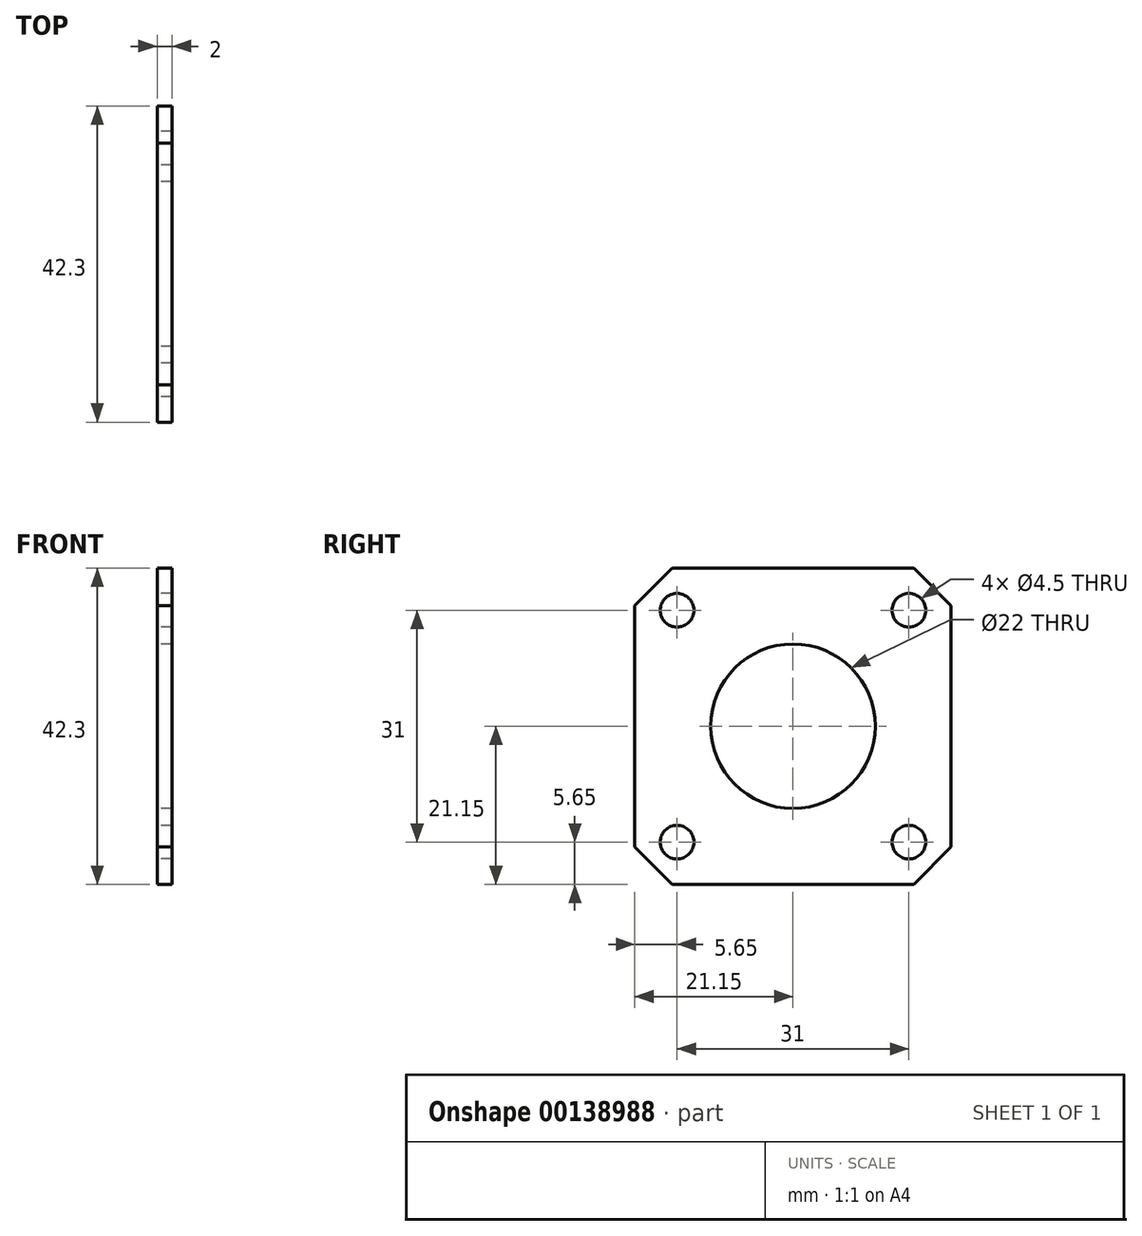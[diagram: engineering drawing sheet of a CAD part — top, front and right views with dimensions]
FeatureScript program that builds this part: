
annotation { "Feature Type Name" : "Feature", "Feature Type Description" : "" }
export const myFeature = defineFeature(function(context is Context, id is Id, definition is map)
    precondition{}
    {
        {
            var Q0;
            Q0=qCreatedBy(makeId("Right.planeOp"),FACE);
            var sketch = newSketch(context, id + "F0", { "sketchPlane" : qUnion([Q0])});
            skLineSegment(sketch, "E0.bottom", {"start": v(21.15, -21.15) * mm, "end": v(-21.15, -21.15) * mm});
            skLineSegment(sketch, "E0.top", {"start": v(21.15, 21.15) * mm, "end": v(-21.15, 21.15) * mm});
            skLineSegment(sketch, "E0.left", {"start": v(21.15, -21.15) * mm, "end": v(21.15, 21.15) * mm});
            skLineSegment(sketch, "E0.right", {"start": v(-21.15, -21.15) * mm, "end": v(-21.15, 21.15) * mm});
            skPoint(sketch, "E0.middle", {"position": v(0, 0) * mm});
            skCircle(sketch, "E1", {"center": v(-15.5, 15.5) * mm, "radius": 2.25 * mm});
            skCircle(sketch, "E2", {"center": v(15.5, 15.5) * mm, "radius": 2.25 * mm});
            skCircle(sketch, "E3", {"center": v(-15.5, -15.5) * mm, "radius": 2.25 * mm});
            skCircle(sketch, "E4", {"center": v(15.5, -15.5) * mm, "radius": 2.25 * mm});
            skCircle(sketch, "E5", {"center": v(0, 0) * mm, "radius": 11 * mm});
            skSolve(sketch);
        }
        {
            var Q0;
            Q0 = qSketchRegion(id + "F0", true);
            extrude(context, id + "F1", {"entities" : qUnion([Q0]), "depth" : 2 * mm});
        }
        {
            var Q0;
            Q0=makeQuery(id+"F1.opExtrude","SWEPT_EDGE",EDGE,{"disambiguationData":[OSD([sQuery(id+"F0.wireOp",EDGE,"E0.top"),sQuery(id+"F0.wireOp",EDGE,"E0.right")])]});
            var Q1;
            Q1=makeQuery(id+"F1.opExtrude","SWEPT_EDGE",EDGE,{"disambiguationData":[OSD([sQuery(id+"F0.wireOp",EDGE,"E0.top"),sQuery(id+"F0.wireOp",EDGE,"E0.left")])]});
            var Q2;
            Q2=makeQuery(id+"F1.opExtrude","SWEPT_EDGE",EDGE,{"disambiguationData":[OSD([sQuery(id+"F0.wireOp",EDGE,"E0.bottom"),sQuery(id+"F0.wireOp",EDGE,"E0.right")])]});
            var Q3;
            Q3=makeQuery(id+"F1.opExtrude","SWEPT_EDGE",EDGE,{"disambiguationData":[OSD([sQuery(id+"F0.wireOp",EDGE,"E0.bottom"),sQuery(id+"F0.wireOp",EDGE,"E0.left")])]});
            chamfer(context, id + "F2", {"entities" : qUnion([Q0, Q1, Q2, Q3]), "width" : 5 * mm, "tangentPropagation" : true});
        }
    });
